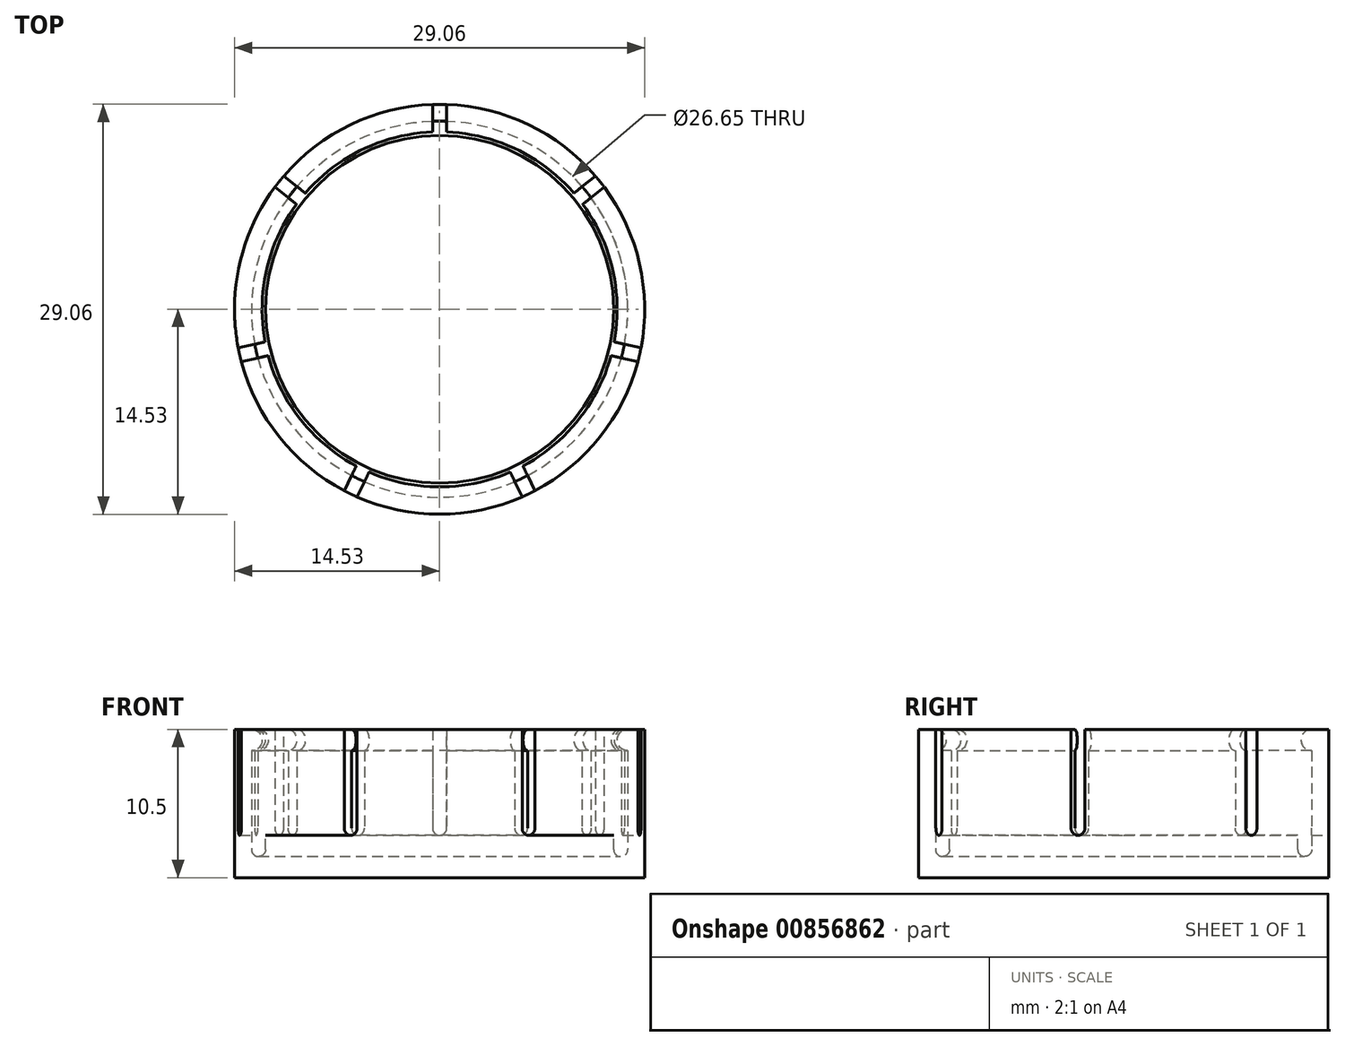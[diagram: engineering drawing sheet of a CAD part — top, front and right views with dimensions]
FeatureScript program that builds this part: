
annotation { "Feature Type Name" : "Feature", "Feature Type Description" : "" }
export const myFeature = defineFeature(function(context is Context, id is Id, definition is map)
    precondition{}
    {
        {
            var Q0;
            Q0=qCreatedBy(makeId("Top.planeOp"),FACE);
            var sketch = newSketch(context, id + "F0", { "sketchPlane" : qUnion([Q0])});
            skCircle(sketch, "E0", {"center": v(0, 0) * mm, "radius": 13.33 * mm});
            skSolve(sketch);
        }
        {
            var Q0;
            Q0=qCreatedBy(makeId("Front.planeOp"),FACE);
            var sketch = newSketch(context, id + "F1", { "sketchPlane" : qUnion([Q0])});
            skPoint(sketch, "E1", {"position": v(13.33, 0) * mm});
            skLineSegment(sketch, "E2", {"start": v(13.33, 0) * mm, "end": v(13.32, 7.5) * mm});
            skLineSegment(sketch, "E3", {"start": v(0, 0) * mm, "end": v(0, 15) * mm, "construction": true});
            skPoint(sketch, "E4", {"position": v(0, 7.5) * mm});
            skLineSegment(sketch, "E5.1", {"start": v(14.53, 0) * mm, "end": v(14.53, 7.5) * mm});
            skLineSegment(sketch, "E6", {"start": v(13.33, 0) * mm, "end": v(14.53, 0) * mm});
            skLineSegment(sketch, "E7", {"start": v(13.32, 7.5) * mm, "end": v(14.53, 7.5) * mm});
            skArc(sketch, "E8", {"start": v(13.32, 7.5) * mm, "mid": v(12.57, 6.75) * mm, "end": v(13.32, 6) * mm});
            skSolve(sketch);
        }
        {
            var Q0;
            Q0=makeQuery(id+"F1.imprint","IMPRINT",FACE,{"disambiguationData":[TD([[makeQuery(id+"F1.imprint","IMPRINT",EDGE,{"derivedFrom":sQuery(id+"F1.wireOp",EDGE,"XOEscWNv-AY5h-7ueE-lvnq-bQ6zLSeS3i4s")}),-1.0]])]});
            var Q1;
            {var subQ0=sQuery(id+"F1.wireOp",EDGE,"E8");Q1=makeQuery(id+"F1.imprint","IMPRINT",FACE,{"disambiguationData":[TD([[makeQuery(id+"F1.imprint","IMPRINT",EDGE,{"derivedFrom":subQ0}),1.0]])]});}
            var Q2;
            Q2=makeQuery(id+"F1.imprint","IMPRINT",FACE,{"disambiguationData":[TD([[makeQuery(id+"F1.imprint","IMPRINT",EDGE,{"derivedFrom":sQuery(id+"F1.wireOp",EDGE,"E5.1")}),1.0]])]});
            var Q3;
            Q3=sQuery(id+"F1.wireOp",EDGE,"E3");
            revolve(context, id + "F2", {"surfaceOperationType" : NewSurfaceOperationType.NEW, "entities" : qUnion([Q0, Q1, Q2]), "axis" : qUnion([Q3]), "revolveType" : RevolveType.FULL});
        }
        {
            var Q0;
            Q0=makeQuery(id+"F2.opRevolve","SWEPT_FACE",FACE,{"disambiguationData":[OSD([sQuery(id+"F1.wireOp",EDGE,"E6")])]});
            var sketch = newSketch(context, id + "F3", { "sketchPlane" : qUnion([Q0])});
            skCircle(sketch, "E9.0", {"center": v(0, 0) * mm, "radius": 14.53 * mm});
            skSolve(sketch);
        }
        {
            var Q0;
            Q0=qSketchRegion(id+"F3",true);
            extrude(context, id + "F4", {"entities" : qUnion([Q0]), "operationType" : NewBodyOperationType.ADD, "depth" : 3 * mm, "offsetDistance" : 25 * mm});
        }
        {
            var Q0;
            Q0=makeQuery(id+"F0.imprint","IMPRINT",FACE,{"disambiguationData":[TD([[makeQuery(id+"F0.imprint","IMPRINT",EDGE,{"derivedFrom":sQuery(id+"F0.wireOp",EDGE,"E0")}),1.0]])]});
            var sketch = newSketch(context, id + "F5", { "sketchPlane" : qUnion([Q0])});
            skLineSegment(sketch, "E10.bottom", {"start": v(0.5, 12.13) * mm, "end": v(-0.5, 12.13) * mm});
            skLineSegment(sketch, "E10.top", {"start": v(0.5, 14.53) * mm, "end": v(-0.5, 14.53) * mm});
            skLineSegment(sketch, "E10.left", {"start": v(0.5, 12.13) * mm, "end": v(0.5, 14.53) * mm});
            skLineSegment(sketch, "E10.right", {"start": v(-0.5, 12.13) * mm, "end": v(-0.5, 14.53) * mm});
            skPoint(sketch, "E10.middle", {"position": v(0, 13.33) * mm});
            skLineSegment(sketch, "E11.1.0", {"start": v(-9.17, 7.95) * mm, "end": v(-11.04, 9.45) * mm});
            skLineSegment(sketch, "E11.1.1", {"start": v(-11.04, 9.45) * mm, "end": v(-11.67, 8.67) * mm});
            skLineSegment(sketch, "E11.1.2", {"start": v(-9.8, 7.17) * mm, "end": v(-11.67, 8.67) * mm});
            skLineSegment(sketch, "E11.1.3", {"start": v(-9.17, 7.95) * mm, "end": v(-9.8, 7.17) * mm});
            skLineSegment(sketch, "E11.2.0", {"start": v(-11.93, -2.21) * mm, "end": v(-14.27, -2.74) * mm});
            skLineSegment(sketch, "E11.2.1", {"start": v(-14.27, -2.74) * mm, "end": v(-14.05, -3.72) * mm});
            skLineSegment(sketch, "E11.2.2", {"start": v(-11.7, -3.19) * mm, "end": v(-14.05, -3.72) * mm});
            skLineSegment(sketch, "E11.2.3", {"start": v(-11.93, -2.21) * mm, "end": v(-11.7, -3.19) * mm});
            skLineSegment(sketch, "E11.3.0", {"start": v(-5.71, -10.7) * mm, "end": v(-6.75, -12.87) * mm});
            skLineSegment(sketch, "E11.3.1", {"start": v(-6.75, -12.87) * mm, "end": v(-5.85, -13.3) * mm});
            skLineSegment(sketch, "E11.3.2", {"start": v(-4.81, -11.14) * mm, "end": v(-5.85, -13.3) * mm});
            skLineSegment(sketch, "E11.3.3", {"start": v(-5.71, -10.7) * mm, "end": v(-4.81, -11.14) * mm});
            skLineSegment(sketch, "E11.4.0", {"start": v(4.81, -11.14) * mm, "end": v(5.85, -13.3) * mm});
            skLineSegment(sketch, "E11.4.1", {"start": v(5.85, -13.3) * mm, "end": v(6.75, -12.87) * mm});
            skLineSegment(sketch, "E11.4.2", {"start": v(5.71, -10.7) * mm, "end": v(6.75, -12.87) * mm});
            skLineSegment(sketch, "E11.4.3", {"start": v(4.81, -11.14) * mm, "end": v(5.71, -10.7) * mm});
            skLineSegment(sketch, "E11.5.0", {"start": v(11.7, -3.19) * mm, "end": v(14.05, -3.72) * mm});
            skLineSegment(sketch, "E11.5.1", {"start": v(14.05, -3.72) * mm, "end": v(14.27, -2.74) * mm});
            skLineSegment(sketch, "E11.5.2", {"start": v(11.93, -2.21) * mm, "end": v(14.27, -2.74) * mm});
            skLineSegment(sketch, "E11.5.3", {"start": v(11.7, -3.19) * mm, "end": v(11.93, -2.21) * mm});
            skLineSegment(sketch, "E11.6.0", {"start": v(9.8, 7.17) * mm, "end": v(11.67, 8.67) * mm});
            skLineSegment(sketch, "E11.6.1", {"start": v(11.67, 8.67) * mm, "end": v(11.04, 9.45) * mm});
            skLineSegment(sketch, "E11.6.2", {"start": v(9.17, 7.95) * mm, "end": v(11.04, 9.45) * mm});
            skLineSegment(sketch, "E11.6.3", {"start": v(9.8, 7.17) * mm, "end": v(9.17, 7.95) * mm});
            skPoint(sketch, "E11.center", {"position": v(0, 0) * mm});
            skSolve(sketch);
        }
        {
            var Q0;
            Q0=qSketchRegion(id+"F5",true);
            extrude(context, id + "F6", {"entities" : qUnion([Q0]), "operationType" : NewBodyOperationType.REMOVE, "depth" : 10 * mm, "offsetDistance" : 25 * mm});
        }
        {
            var Q0;
            Q0=makeQuery(id+"F0.imprint","IMPRINT",FACE,{"disambiguationData":[TD([[makeQuery(id+"F0.imprint","IMPRINT",EDGE,{"derivedFrom":sQuery(id+"F0.wireOp",EDGE,"E0")}),1.0]])]});
            var sketch = newSketch(context, id + "F7", { "sketchPlane" : qUnion([Q0])});
            skCircle(sketch, "E12.0", {"center": v(0, 0) * mm, "radius": 12.32 * mm});
            skCircle(sketch, "E13.0", {"center": v(0, 0) * mm, "radius": 13.33 * mm});
            skSolve(sketch);
        }
        {
            var Q0;
            Q0=makeQuery(id+"F7.imprint","IMPRINT",FACE,{"disambiguationData":[TD([[makeQuery(id+"F7.imprint","IMPRINT",EDGE,{"derivedFrom":sQuery(id+"F7.wireOp",EDGE,"E12.0")}),-1.0]])]});
            extrude(context, id + "F8", {"entities" : qUnion([Q0]), "operationType" : NewBodyOperationType.REMOVE, "oppositeDirection" : true, "depth" : 1.5 * mm, "offsetDistance" : 25 * mm});
        }
        {
            var Q0;
            Q0=makeQuery(id+"F8.boolean.opBoolean","COPY",EDGE,{"derivedFrom":makeQuery(id+"F8.opExtrude","CAP_EDGE",EDGE,{"disambiguationData":[OSD([sQuery(id+"F7.wireOp",EDGE,"E13.0")])],"isStart":false})});
            var Q1;
            Q1=makeQuery(id+"F8.boolean.opBoolean","COPY",EDGE,{"derivedFrom":makeQuery(id+"F8.opExtrude","CAP_EDGE",EDGE,{"disambiguationData":[OSD([sQuery(id+"F7.wireOp",EDGE,"E12.0")])],"isStart":false})});
            var Q2;
            Q2=makeQuery(id+"F6.boolean.opBoolean","COPY",EDGE,{"derivedFrom":makeQuery(id+"F6.opExtrude","CAP_EDGE",EDGE,{"disambiguationData":[OSD([sQuery(id+"F5.wireOp",EDGE,"E11.2.2")])],"isStart":true})});
            var Q3;
            Q3=makeQuery(id+"F6.boolean.opBoolean","COPY",EDGE,{"derivedFrom":makeQuery(id+"F6.opExtrude","CAP_EDGE",EDGE,{"disambiguationData":[OSD([sQuery(id+"F5.wireOp",EDGE,"E11.2.0")])],"isStart":true})});
            var Q4;
            Q4=makeQuery(id+"F6.boolean.opBoolean","COPY",EDGE,{"derivedFrom":makeQuery(id+"F6.opExtrude","CAP_EDGE",EDGE,{"disambiguationData":[OSD([sQuery(id+"F5.wireOp",EDGE,"E11.3.2")])],"isStart":true})});
            var Q5;
            Q5=makeQuery(id+"F6.boolean.opBoolean","COPY",EDGE,{"derivedFrom":makeQuery(id+"F6.opExtrude","CAP_EDGE",EDGE,{"disambiguationData":[OSD([sQuery(id+"F5.wireOp",EDGE,"E11.3.0")])],"isStart":true})});
            var Q6;
            Q6=makeQuery(id+"F6.boolean.opBoolean","COPY",EDGE,{"derivedFrom":makeQuery(id+"F6.opExtrude","CAP_EDGE",EDGE,{"disambiguationData":[OSD([sQuery(id+"F5.wireOp",EDGE,"E11.4.2")])],"isStart":true})});
            var Q7;
            Q7=makeQuery(id+"F6.boolean.opBoolean","COPY",EDGE,{"derivedFrom":makeQuery(id+"F6.opExtrude","CAP_EDGE",EDGE,{"disambiguationData":[OSD([sQuery(id+"F5.wireOp",EDGE,"E11.4.0")])],"isStart":true})});
            var Q8;
            Q8=makeQuery(id+"F6.boolean.opBoolean","COPY",EDGE,{"derivedFrom":makeQuery(id+"F6.opExtrude","CAP_EDGE",EDGE,{"disambiguationData":[OSD([sQuery(id+"F5.wireOp",EDGE,"E11.1.2")])],"isStart":true})});
            var Q9;
            Q9=makeQuery(id+"F6.boolean.opBoolean","COPY",EDGE,{"derivedFrom":makeQuery(id+"F6.opExtrude","CAP_EDGE",EDGE,{"disambiguationData":[OSD([sQuery(id+"F5.wireOp",EDGE,"E11.1.0")])],"isStart":true})});
            var Q10;
            Q10=makeQuery(id+"F6.boolean.opBoolean","COPY",EDGE,{"derivedFrom":makeQuery(id+"F6.opExtrude","CAP_EDGE",EDGE,{"disambiguationData":[OSD([sQuery(id+"F5.wireOp",EDGE,"E10.left")])],"isStart":true})});
            var Q11;
            Q11=makeQuery(id+"F6.boolean.opBoolean","COPY",EDGE,{"derivedFrom":makeQuery(id+"F6.opExtrude","CAP_EDGE",EDGE,{"disambiguationData":[OSD([sQuery(id+"F5.wireOp",EDGE,"E10.right")])],"isStart":true})});
            var Q12;
            Q12=makeQuery(id+"F6.boolean.opBoolean","COPY",EDGE,{"derivedFrom":makeQuery(id+"F6.opExtrude","CAP_EDGE",EDGE,{"disambiguationData":[OSD([sQuery(id+"F5.wireOp",EDGE,"E11.6.0")])],"isStart":true})});
            var Q13;
            Q13=makeQuery(id+"F6.boolean.opBoolean","COPY",EDGE,{"derivedFrom":makeQuery(id+"F6.opExtrude","CAP_EDGE",EDGE,{"disambiguationData":[OSD([sQuery(id+"F5.wireOp",EDGE,"E11.6.2")])],"isStart":true})});
            var Q14;
            Q14=makeQuery(id+"F6.boolean.opBoolean","COPY",EDGE,{"derivedFrom":makeQuery(id+"F6.opExtrude","CAP_EDGE",EDGE,{"disambiguationData":[OSD([sQuery(id+"F5.wireOp",EDGE,"E11.5.0")])],"isStart":true})});
            var Q15;
            Q15=makeQuery(id+"F6.boolean.opBoolean","COPY",EDGE,{"derivedFrom":makeQuery(id+"F6.opExtrude","CAP_EDGE",EDGE,{"disambiguationData":[OSD([sQuery(id+"F5.wireOp",EDGE,"E11.5.2")])],"isStart":true})});
            fillet(context, id + "F9", {"entities" : qUnion([Q0, Q1, Q2, Q3, Q4, Q5, Q6, Q7, Q8, Q9, Q10, Q11, Q12, Q13, Q14, Q15]), "radius" : 0.5 * mm, "tangentPropagation" : true, "allowEdgeOverflow" : false});
        }
    });
